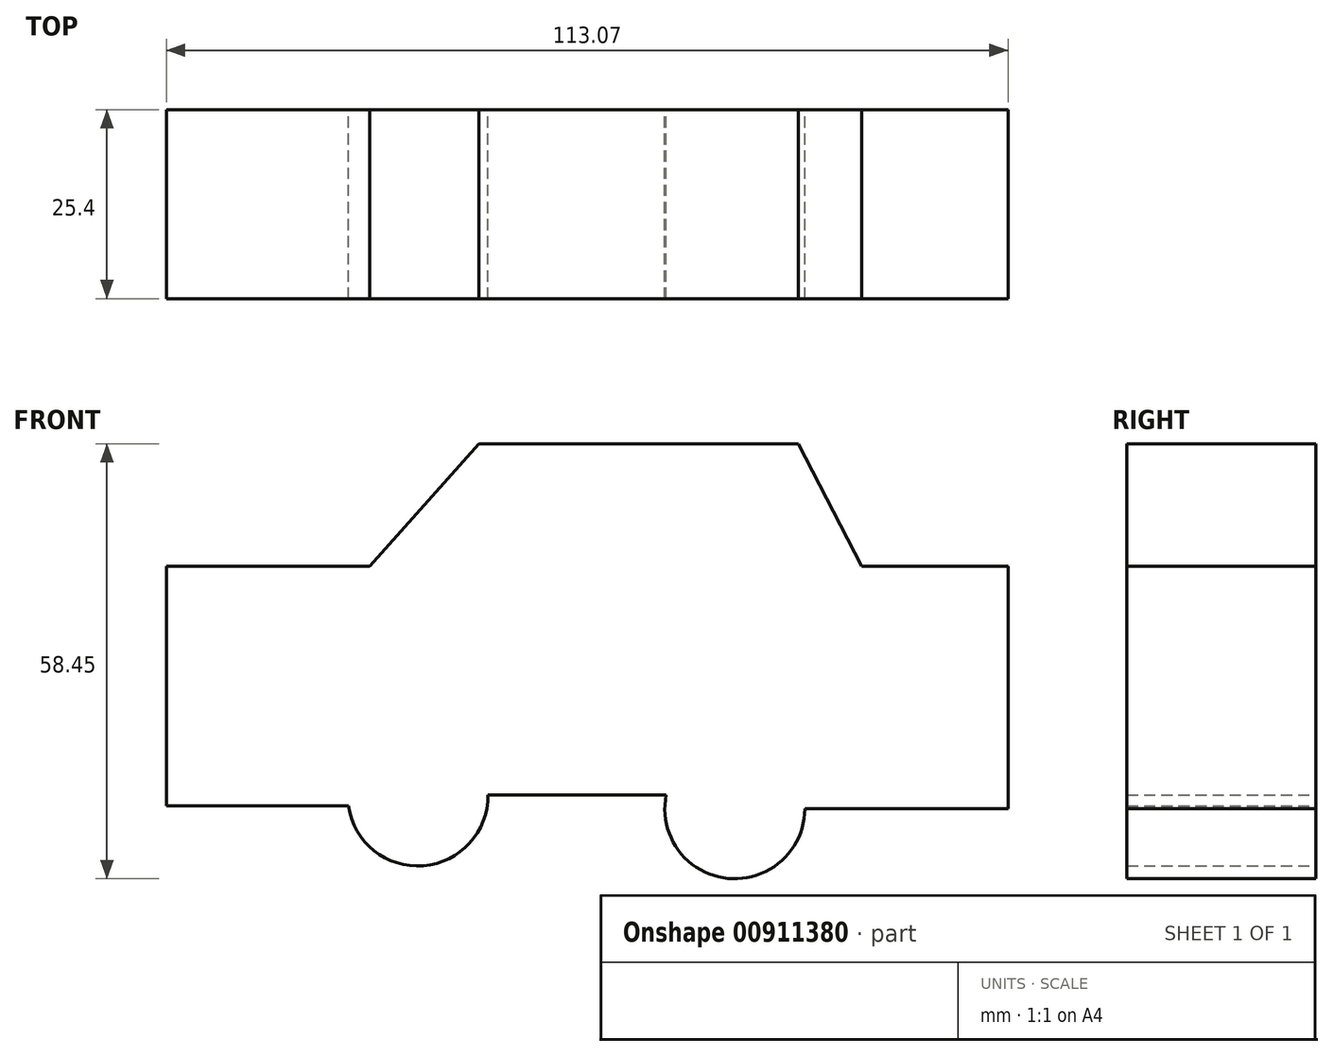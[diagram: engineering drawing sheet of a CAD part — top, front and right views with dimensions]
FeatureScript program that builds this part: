
annotation { "Feature Type Name" : "Feature", "Feature Type Description" : "" }
export const myFeature = defineFeature(function(context is Context, id is Id, definition is map)
    precondition{}
    {
        {
            var Q0;
            Q0=qCreatedBy(makeId("Front.planeOp"),FACE);
            var sketch = newSketch(context, id + "F0", { "sketchPlane" : qUnion([Q0])});
            skPoint(sketch, "E0.start.orphan", {"position": v(-35.19, 14.45) * mm});
            skPoint(sketch, "E1.end.orphan", {"position": v(-35.19, -5.4) * mm});
            skPoint(sketch, "E2.end.orphan", {"position": v(-35.19, 34.31) * mm});
            skPoint(sketch, "E3.end.orphan", {"position": v(-35.19, -7.74) * mm});
            skLineSegment(sketch, "E4", {"start": v(-55.07, -7.74) * mm, "end": v(-55.07, 24.48) * mm});
            skLineSegment(sketch, "E5", {"start": v(-55.07, 24.48) * mm, "end": v(-27.76, 24.48) * mm});
            skLineSegment(sketch, "E6", {"start": v(-27.76, 24.48) * mm, "end": v(-13.07, 40.93) * mm});
            skLineSegment(sketch, "E7", {"start": v(-13.07, 40.93) * mm, "end": v(29.8, 40.93) * mm});
            skLineSegment(sketch, "E8", {"start": v(29.8, 40.93) * mm, "end": v(38.32, 24.48) * mm});
            skLineSegment(sketch, "E9", {"start": v(38.32, 24.48) * mm, "end": v(58, 24.48) * mm});
            skLineSegment(sketch, "E10", {"start": v(58, 24.48) * mm, "end": v(58, -8.12) * mm});
            skPoint(sketch, "E11.start.orphan", {"position": v(-12.49, -8.12) * mm});
            skPoint(sketch, "E12.end.orphan", {"position": v(37.15, -8.12) * mm});
            skCircle(sketch, "E13", {"center": v(-21.3, -6.35) * mm, "radius": 9.44 * mm});
            skPoint(sketch, "E14.center.orphan", {"position": v(21.3, -8.12) * mm});
            skCircle(sketch, "E15", {"center": v(21.3, -8.12) * mm, "radius": 9.4 * mm});
            skLineSegment(sketch, "E16", {"start": v(-11.86, -6.26) * mm, "end": v(12.07, -6.26) * mm});
            skLineSegment(sketch, "E17", {"start": v(30.7, -8.12) * mm, "end": v(58, -8.12) * mm});
            skLineSegment(sketch, "E18", {"start": v(-55.07, -7.74) * mm, "end": v(-30.63, -7.74) * mm});
            skSolve(sketch);
        }
        {
            var Q0;
            {var subQ0=sQuery(id+"F0.wireOp",EDGE,"E13");var subQ1=makeQuery(id+"F0.imprint","INTERSECT",VERTEX,{"derivedFrom":[subQ0,sQuery(id+"F0.wireOp",EDGE,"E16")]});Q0=makeQuery(id+"F0.imprint","IMPRINT",FACE,{"disambiguationData":[TD([[makeQuery(id+"F0.imprint","IMPRINT",EDGE,{"disambiguationData":[TD([[subQ1,-1.0]])],"derivedFrom":subQ0}),1.0]])]});}
            var Q1;
            {var subQ0=sQuery(id+"F0.wireOp",EDGE,"E15");var subQ1=makeQuery(id+"F0.imprint","INTERSECT",VERTEX,{"derivedFrom":[subQ0,sQuery(id+"F0.wireOp",EDGE,"E16")]});Q1=makeQuery(id+"F0.imprint","IMPRINT",FACE,{"disambiguationData":[TD([[makeQuery(id+"F0.imprint","IMPRINT",EDGE,{"disambiguationData":[TD([[subQ1,1.0]])],"derivedFrom":subQ0}),1.0]])]});}
            var Q2;
            Q2=makeQuery(id+"F0.imprint","IMPRINT",FACE,{"disambiguationData":[TD([[makeQuery(id+"F0.imprint","IMPRINT",EDGE,{"derivedFrom":sQuery(id+"F0.wireOp",EDGE,"E4")}),-1.0]])]});
            extrude(context, id + "F1", {"entities" : qUnion([Q0, Q1, Q2]), "depth" : 25.4 * mm, "offsetDistance" : 25.4 * mm});
        }
    });
